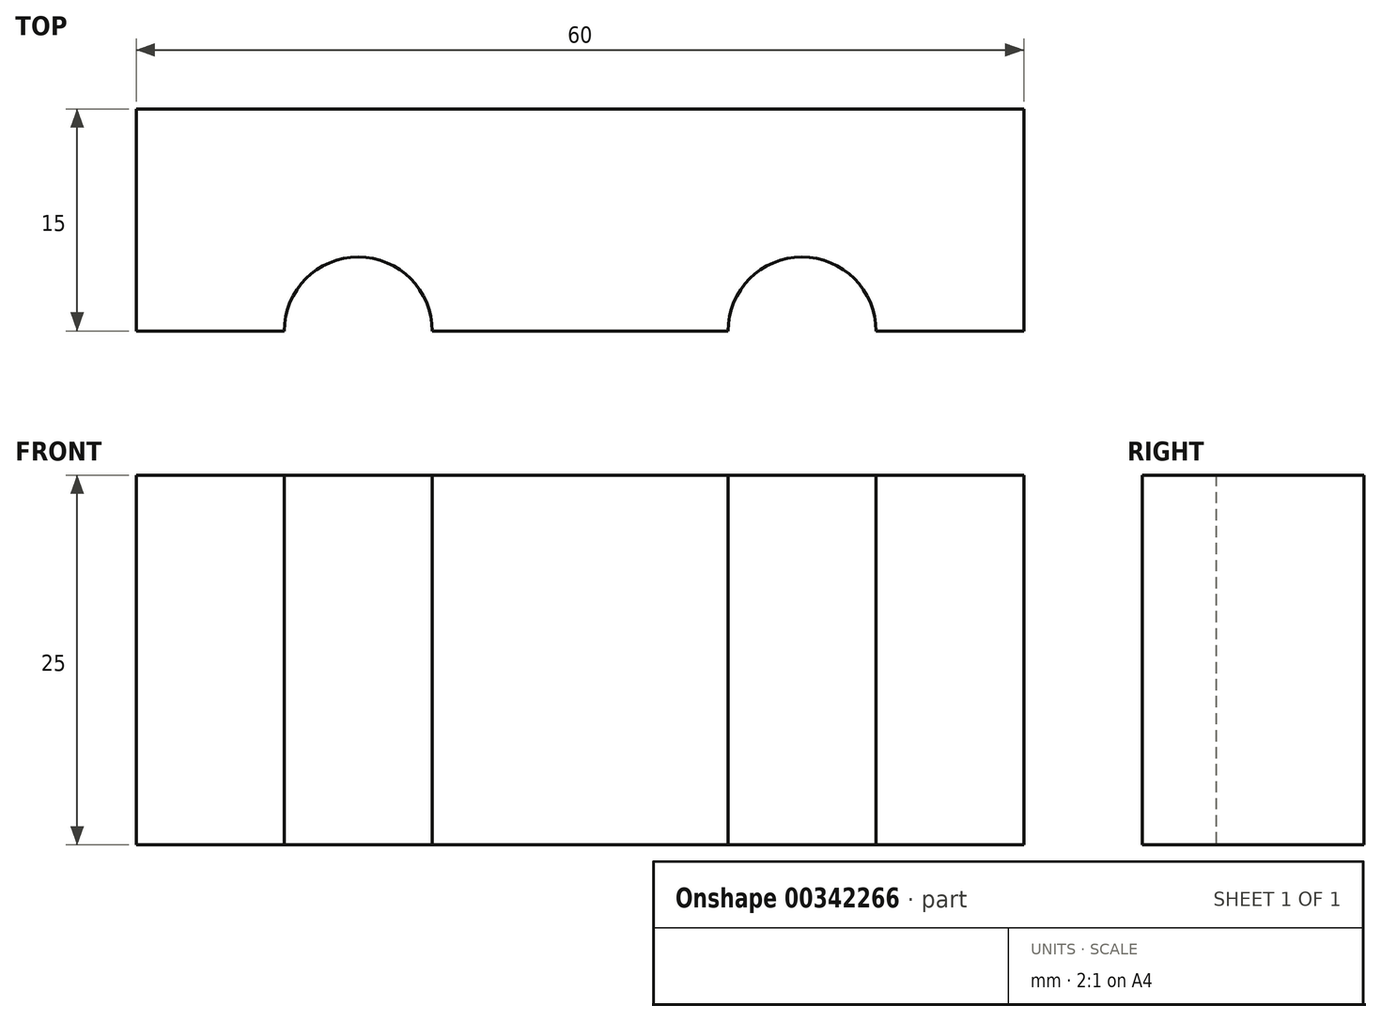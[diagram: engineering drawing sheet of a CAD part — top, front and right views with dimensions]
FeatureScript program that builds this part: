
annotation { "Feature Type Name" : "Feature", "Feature Type Description" : "" }
export const myFeature = defineFeature(function(context is Context, id is Id, definition is map)
    precondition{}
    {
        {
            var Q0;
            Q0=qCreatedBy(makeId("Top.planeOp"),FACE);
            var sketch = newSketch(context, id + "F0", { "sketchPlane" : qUnion([Q0])});
            skLineSegment(sketch, "E0", {"start": v(-65.2, -16.37) * mm, "end": v(-5.2, -16.37) * mm});
            skLineSegment(sketch, "E1", {"start": v(-5.2, -16.37) * mm, "end": v(-5.2, -31.37) * mm});
            skLineSegment(sketch, "E2", {"start": v(-5.2, -31.37) * mm, "end": v(-65.2, -31.37) * mm});
            skLineSegment(sketch, "E3", {"start": v(-65.2, -31.37) * mm, "end": v(-65.2, -16.37) * mm});
            skCircle(sketch, "E4", {"center": v(-50.2, -31.37) * mm, "radius": 5 * mm});
            skCircle(sketch, "E5", {"center": v(-20.2, -31.37) * mm, "radius": 5 * mm});
            skSolve(sketch);
        }
        {
            var Q0;
            Q0=makeQuery(id+"F0.imprint","IMPRINT",FACE,{"disambiguationData":[TD([[makeQuery(id+"F0.imprint","IMPRINT",EDGE,{"derivedFrom":sQuery(id+"F0.wireOp",EDGE,"E0")}),-1.0]])]});
            extrude(context, id + "F1", {"entities" : qUnion([Q0]), "depth" : 25 * mm});
        }
    });
